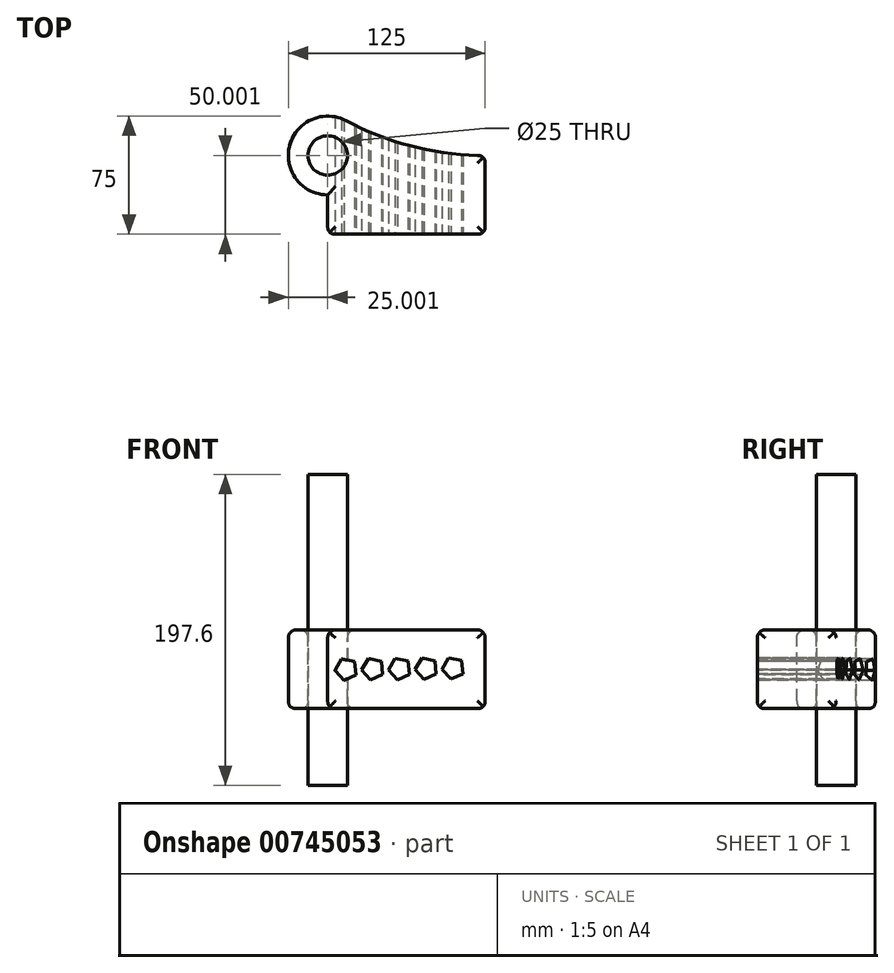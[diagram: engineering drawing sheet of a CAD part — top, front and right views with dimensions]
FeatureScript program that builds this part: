
annotation { "Feature Type Name" : "Feature", "Feature Type Description" : "" }
export const myFeature = defineFeature(function(context is Context, id is Id, definition is map)
    precondition{}
    {
        {
            var Q0;
            Q0=qCreatedBy(makeId("Top.planeOp"),FACE);
            var sketch = newSketch(context, id + "F0", { "sketchPlane" : qUnion([Q0])});
            skLineSegment(sketch, "E0.bottom", {"start": v(-52.2, 21.67) * mm, "end": v(47.8, 21.67) * mm});
            skLineSegment(sketch, "E0.top", {"start": v(-52.2, -28.33) * mm, "end": v(47.8, -28.33) * mm});
            skLineSegment(sketch, "E0.left", {"start": v(-52.2, 21.67) * mm, "end": v(-52.2, -28.33) * mm});
            skLineSegment(sketch, "E0.right", {"start": v(47.8, 21.67) * mm, "end": v(47.8, -28.33) * mm});
            skCircle(sketch, "E1", {"center": v(-52.2, 21.67) * mm, "radius": 25 * mm});
            skArc(sketch, "E2", {"start": v(-40.44, 43.73) * mm, "mid": v(2.32, 27.27) * mm, "end": v(47.8, 21.67) * mm});
            skCircle(sketch, "E3", {"center": v(-52.2, 21.67) * mm, "radius": 12.5 * mm});
            skSolve(sketch);
        }
        {
            var Q0;
            {var subQ4=sQuery(id+"F0.wireOp",EDGE,"E0.bottom");var subQ6=sQuery(id+"F0.wireOp",EDGE,"E3");var subQ8=makeQuery(id+"F0.imprint","INTERSECT",VERTEX,{"derivedFrom":[subQ4,subQ6]});Q0=makeQuery(id+"F0.imprint","IMPRINT",FACE,{"disambiguationData":[TD([[makeQuery(id+"F0.imprint","IMPRINT",EDGE,{"disambiguationData":[TD([[subQ8,-1.0]])],"derivedFrom":subQ4}),1.0]])]});}
            var Q1;
            {var subQ1=sQuery(id+"F0.wireOp",EDGE,"E0.top");Q1=makeQuery(id+"F0.imprint","IMPRINT",FACE,{"disambiguationData":[TD([[makeQuery(id+"F0.imprint","IMPRINT",EDGE,{"derivedFrom":subQ1}),1.0]])]});}
            var Q2;
            {var subQ0=sQuery(id+"F0.wireOp",EDGE,"E2");Q2=makeQuery(id+"F0.imprint","IMPRINT",FACE,{"disambiguationData":[TD([[makeQuery(id+"F0.imprint","IMPRINT",EDGE,{"derivedFrom":subQ0}),-1.0]])]});}
            var Q3;
            {var subQ0=sQuery(id+"F0.wireOp",EDGE,"E3");var subQ1=sQuery(id+"F0.wireOp",EDGE,"E0.bottom");var subQ2=makeQuery(id+"F0.imprint","INTERSECT",VERTEX,{"derivedFrom":[subQ1,subQ0]});Q3=makeQuery(id+"F0.imprint","IMPRINT",FACE,{"disambiguationData":[TD([[makeQuery(id+"F0.imprint","IMPRINT",EDGE,{"disambiguationData":[TD([[subQ2,-1.0]])],"derivedFrom":subQ1}),-1.0]])]});}
            extrude(context, id + "F1", {"entities" : qUnion([Q0, Q1, Q2, Q3]), "oppositeDirection" : true, "depth" : 50 * mm, "offsetDistance" : 25 * mm});
        }
        {
            var Q0;
            {var subQ0=sQuery(id+"F0.wireOp",EDGE,"E0.left");var subQ1=sQuery(id+"F0.wireOp",EDGE,"E0.bottom");var subQ2=makeQuery(id+"F0.imprint","INTERSECT",VERTEX,{"derivedFrom":[subQ1,subQ0]});Q0=makeQuery(id+"F0.imprint","IMPRINT",FACE,{"disambiguationData":[TD([[makeQuery(id+"F0.imprint","IMPRINT",EDGE,{"disambiguationData":[TD([[subQ2,-1.0]])],"derivedFrom":subQ1}),1.0]])]});}
            var Q1;
            {var subQ0=sQuery(id+"F0.wireOp",EDGE,"E0.left");var subQ1=sQuery(id+"F0.wireOp",EDGE,"E0.bottom");var subQ2=makeQuery(id+"F0.imprint","INTERSECT",VERTEX,{"derivedFrom":[subQ1,subQ0]});Q1=makeQuery(id+"F0.imprint","IMPRINT",FACE,{"disambiguationData":[TD([[makeQuery(id+"F0.imprint","IMPRINT",EDGE,{"disambiguationData":[TD([[subQ2,-1.0]])],"derivedFrom":subQ1}),-1.0]])]});}
            var Q2;
            Q2=sQuery(id+"F0.wireOp",EDGE,"E3");
            extrude(context, id + "F2", {"entities" : qUnion([Q0, Q1]), "surfaceEntities" : qUnion([Q2]), "endBound" : BoundingType.SYMMETRIC, "depth" : 197.6 * mm, "offsetDistance" : 25 * mm});
        }
        {
            var Q0;
            Q0=makeQuery(id+"F1.opExtrude","SWEPT_FACE",FACE,{"disambiguationData":[OSD([sQuery(id+"F0.wireOp",EDGE,"E0.top")])]});
            var sketch = newSketch(context, id + "F3", { "sketchPlane" : qUnion([Q0])});
            skPoint(sketch, "E4.cCircle.centerSnap0", {"position": v(-52.2, -25) * mm});
            skCircle(sketch, "E5.cCircle", {"center": v(-40.49, -25) * mm, "radius": 5.79 * mm, "construction": true});
            skLineSegment(sketch, "E5.0", {"start": v(-47.6, -25.76) * mm, "end": v(-43.4, -18.47) * mm});
            skLineSegment(sketch, "E5.1", {"start": v(-43.4, -18.47) * mm, "end": v(-35.18, -20.2) * mm});
            skLineSegment(sketch, "E5.2", {"start": v(-35.18, -20.2) * mm, "end": v(-34.29, -28.57) * mm});
            skLineSegment(sketch, "E5.3", {"start": v(-34.29, -28.57) * mm, "end": v(-41.96, -32) * mm});
            skLineSegment(sketch, "E5.4", {"start": v(-41.96, -32) * mm, "end": v(-47.6, -25.76) * mm});
            skPoint(sketch, "E5.0.midPoint", {"position": v(-45.5, -22.12) * mm});
            skLineSegment(sketch, "E6.1.0.0", {"start": v(-26.4, -18.3) * mm, "end": v(-18.18, -20.03) * mm});
            skCircle(sketch, "E6.1.0.1", {"center": v(-23.49, -24.83) * mm, "radius": 5.79 * mm, "construction": true});
            skLineSegment(sketch, "E6.1.0.2", {"start": v(-18.18, -20.03) * mm, "end": v(-17.29, -28.4) * mm});
            skLineSegment(sketch, "E6.1.0.3", {"start": v(-17.29, -28.4) * mm, "end": v(-24.96, -31.83) * mm});
            skPoint(sketch, "E6.1.0.4", {"position": v(-28.5, -21.95) * mm});
            skLineSegment(sketch, "E6.1.0.5", {"start": v(-30.6, -25.6) * mm, "end": v(-26.4, -18.3) * mm});
            skLineSegment(sketch, "E6.1.0.6", {"start": v(-24.96, -31.83) * mm, "end": v(-30.6, -25.6) * mm});
            skLineSegment(sketch, "E6.2.0.0", {"start": v(-9.4, -18.13) * mm, "end": v(-1.18, -19.86) * mm});
            skCircle(sketch, "E6.2.0.1", {"center": v(-6.49, -24.66) * mm, "radius": 5.79 * mm, "construction": true});
            skLineSegment(sketch, "E6.2.0.2", {"start": v(-1.18, -19.86) * mm, "end": v(-0.29, -28.23) * mm});
            skLineSegment(sketch, "E6.2.0.3", {"start": v(-0.29, -28.23) * mm, "end": v(-7.96, -31.66) * mm});
            skPoint(sketch, "E6.2.0.4", {"position": v(-11.5, -21.78) * mm});
            skLineSegment(sketch, "E6.2.0.5", {"start": v(-13.6, -25.42) * mm, "end": v(-9.4, -18.13) * mm});
            skLineSegment(sketch, "E6.2.0.6", {"start": v(-7.96, -31.66) * mm, "end": v(-13.6, -25.42) * mm});
            skLineSegment(sketch, "E6.3.0.0", {"start": v(7.59, -17.96) * mm, "end": v(15.82, -19.7) * mm});
            skCircle(sketch, "E6.3.0.1", {"center": v(10.51, -24.5) * mm, "radius": 5.79 * mm, "construction": true});
            skLineSegment(sketch, "E6.3.0.2", {"start": v(15.82, -19.7) * mm, "end": v(16.71, -28.06) * mm});
            skLineSegment(sketch, "E6.3.0.3", {"start": v(16.71, -28.06) * mm, "end": v(9.04, -31.49) * mm});
            skPoint(sketch, "E6.3.0.4", {"position": v(5.5, -21.6) * mm});
            skLineSegment(sketch, "E6.3.0.5", {"start": v(3.4, -25.25) * mm, "end": v(7.59, -17.96) * mm});
            skLineSegment(sketch, "E6.3.0.6", {"start": v(9.04, -31.49) * mm, "end": v(3.4, -25.25) * mm});
            skLineSegment(sketch, "E6.4.0.0", {"start": v(24.59, -17.8) * mm, "end": v(32.82, -19.52) * mm});
            skCircle(sketch, "E6.4.0.1", {"center": v(27.5, -24.32) * mm, "radius": 5.79 * mm, "construction": true});
            skLineSegment(sketch, "E6.4.0.2", {"start": v(32.82, -19.52) * mm, "end": v(33.71, -27.89) * mm});
            skLineSegment(sketch, "E6.4.0.3", {"start": v(33.71, -27.89) * mm, "end": v(26.04, -31.32) * mm});
            skPoint(sketch, "E6.4.0.4", {"position": v(22.5, -21.44) * mm});
            skLineSegment(sketch, "E6.4.0.5", {"start": v(20.4, -25.08) * mm, "end": v(24.59, -17.8) * mm});
            skLineSegment(sketch, "E6.4.0.6", {"start": v(26.04, -31.32) * mm, "end": v(20.4, -25.08) * mm});
            skLineSegment(sketch, "E6.direction1", {"start": v(-41.96, -32) * mm, "end": v(-24.96, -31.83) * mm, "construction": true});
            skSolve(sketch);
        }
        {
            var Q0;
            Q0=makeQuery(id+"F3.imprint","IMPRINT",FACE,{"disambiguationData":[TD([[makeQuery(id+"F3.imprint","IMPRINT",EDGE,{"derivedFrom":sQuery(id+"F3.wireOp",EDGE,"E5.0")}),-1.0]])]});
            var Q1;
            Q1=makeQuery(id+"F3.imprint","IMPRINT",FACE,{"disambiguationData":[TD([[makeQuery(id+"F3.imprint","IMPRINT",EDGE,{"derivedFrom":sQuery(id+"F3.wireOp",EDGE,"E6.2.0.0")}),-1.0]])]});
            var Q2;
            Q2=makeQuery(id+"F3.imprint","IMPRINT",FACE,{"disambiguationData":[TD([[makeQuery(id+"F3.imprint","IMPRINT",EDGE,{"derivedFrom":sQuery(id+"F3.wireOp",EDGE,"E6.3.0.0")}),-1.0]])]});
            var Q3;
            Q3=makeQuery(id+"F3.imprint","IMPRINT",FACE,{"disambiguationData":[TD([[makeQuery(id+"F3.imprint","IMPRINT",EDGE,{"derivedFrom":sQuery(id+"F3.wireOp",EDGE,"E6.4.0.0")}),-1.0]])]});
            var Q4;
            Q4=makeQuery(id+"F3.imprint","IMPRINT",FACE,{"disambiguationData":[TD([[makeQuery(id+"F3.imprint","IMPRINT",EDGE,{"derivedFrom":sQuery(id+"F3.wireOp",EDGE,"E6.1.0.0")}),-1.0]])]});
            extrude(context, id + "F4", {"entities" : qUnion([Q0, Q1, Q2, Q3, Q4]), "operationType" : NewBodyOperationType.REMOVE, "endBound" : BoundingType.THROUGH_ALL, "oppositeDirection" : true, "depth" : 92.8 * mm, "offsetDistance" : 25 * mm});
        }
        {
            var Q0;
            Q0=makeQuery(id+"F1.opExtrude","CAP_FACE",FACE,{"disambiguationData":[OSD([sQuery(id+"F0.wireOp",EDGE,"E0.top"),sQuery(id+"F0.wireOp",EDGE,"E0.left"),sQuery(id+"F0.wireOp",EDGE,"E0.right"),sQuery(id+"F0.wireOp",EDGE,"E1"),sQuery(id+"F0.wireOp",EDGE,"E2"),sQuery(id+"F0.wireOp",EDGE,"E3")])],"isStart":true});
            fillet(context, id + "F5", {"entities" : qUnion([Q0]), "radius" : 5 * mm, "tangentPropagation" : true, "allowEdgeOverflow" : false});
        }
        {
            var Q0;
            Q0=makeQuery(id+"F1.opExtrude","CAP_FACE",FACE,{"disambiguationData":[OSD([sQuery(id+"F0.wireOp",EDGE,"E0.top"),sQuery(id+"F0.wireOp",EDGE,"E0.left"),sQuery(id+"F0.wireOp",EDGE,"E0.right"),sQuery(id+"F0.wireOp",EDGE,"E1"),sQuery(id+"F0.wireOp",EDGE,"E2"),sQuery(id+"F0.wireOp",EDGE,"E3")])],"isStart":false});
            fillet(context, id + "F6", {"entities" : qUnion([Q0]), "radius" : 5 * mm, "tangentPropagation" : true, "rho" : 0.5, "crossSection" : FilletCrossSection.CONIC, "allowEdgeOverflow" : false});
        }
        {
            var Q0;
            Q0=makeQuery(id+"F1.opExtrude","SWEPT_EDGE",EDGE,{"disambiguationData":[OSD([sQuery(id+"F0.wireOp",EDGE,"E0.top"),sQuery(id+"F0.wireOp",EDGE,"E0.left")])]});
            var Q1;
            Q1=makeQuery(id+"F1.opExtrude","SWEPT_EDGE",EDGE,{"disambiguationData":[OSD([sQuery(id+"F0.wireOp",EDGE,"E0.top"),sQuery(id+"F0.wireOp",EDGE,"E0.right")])]});
            var Q2;
            Q2=makeQuery(id+"F1.opExtrude","SWEPT_EDGE",EDGE,{"disambiguationData":[OSD([sQuery(id+"F0.wireOp",EDGE,"E0.bottom"),sQuery(id+"F0.wireOp",EDGE,"E0.right"),sQuery(id+"F0.wireOp",EDGE,"E2")])]});
            fillet(context, id + "F7", {"entities" : qUnion([Q0, Q1, Q2]), "radius" : 5 * mm, "rho" : 0.5, "crossSection" : FilletCrossSection.CONIC, "allowEdgeOverflow" : false});
        }
    });
